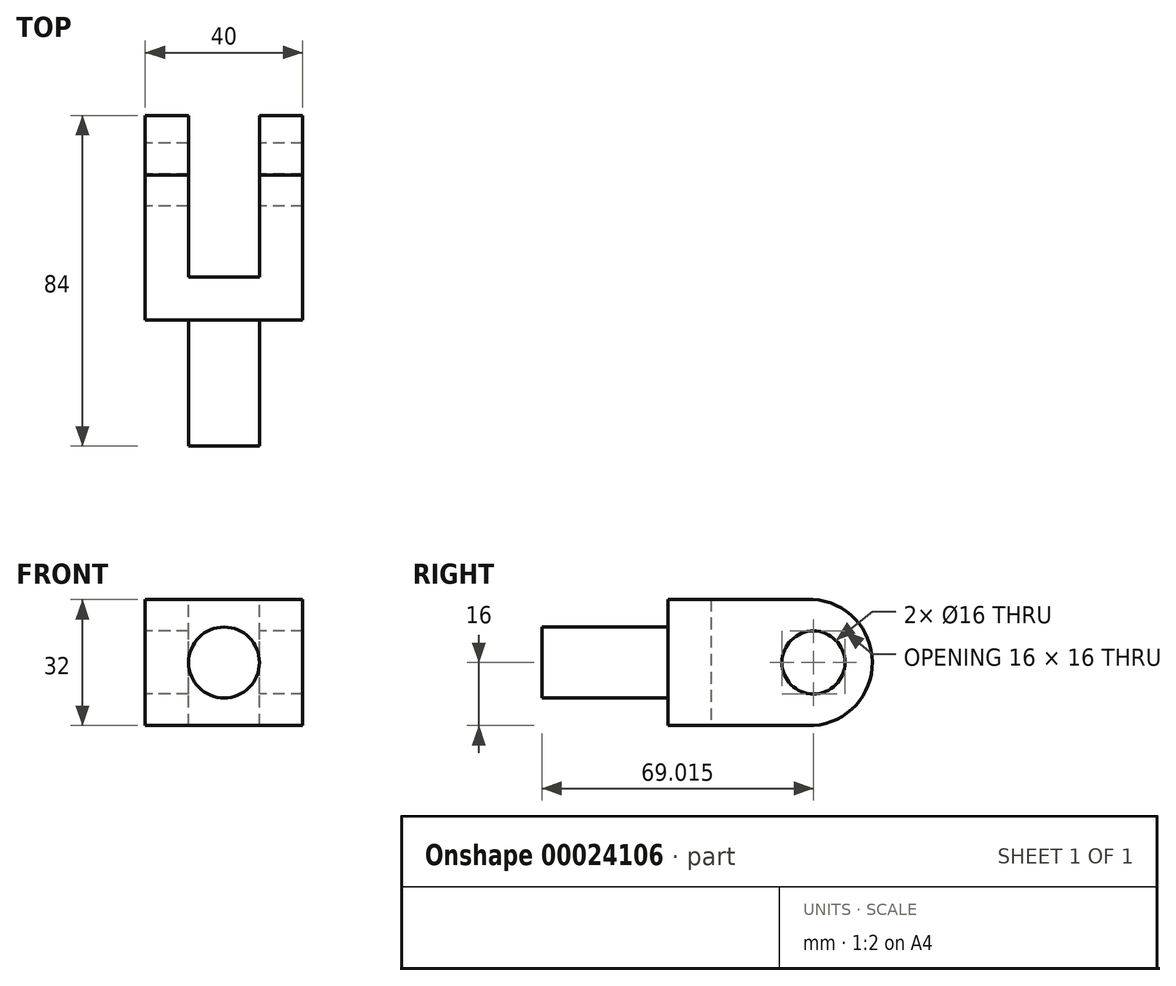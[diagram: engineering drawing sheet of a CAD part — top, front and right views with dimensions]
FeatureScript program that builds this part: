
annotation { "Feature Type Name" : "Feature", "Feature Type Description" : "" }
export const myFeature = defineFeature(function(context is Context, id is Id, definition is map)
    precondition{}
    {
        {
            var Q0;
            Q0=qCreatedBy(makeId("Top.planeOp"),FACE);
            var sketch = newSketch(context, id + "F0", { "sketchPlane" : qUnion([Q0])});
            skLineSegment(sketch, "E0", {"start": v(-30.3, 35) * mm, "end": v(-30.3, -17) * mm});
            skLineSegment(sketch, "E1", {"start": v(-30.3, -17) * mm, "end": v(9.7, -17) * mm});
            skLineSegment(sketch, "E2", {"start": v(9.7, -17) * mm, "end": v(9.7, 35) * mm});
            skLineSegment(sketch, "E3", {"start": v(-30.3, 35) * mm, "end": v(-19.3, 35) * mm});
            skLineSegment(sketch, "E4", {"start": v(9.7, 35) * mm, "end": v(-1.3, 35) * mm});
            skLineSegment(sketch, "E5", {"start": v(-19.3, 35) * mm, "end": v(-19.3, -6) * mm});
            skLineSegment(sketch, "E6", {"start": v(-1.3, 35) * mm, "end": v(-1.3, -6) * mm});
            skLineSegment(sketch, "E7", {"start": v(-19.3, -6) * mm, "end": v(-1.3, -6) * mm});
            skSolve(sketch);
        }
        {
            var Q0;
            Q0=qSketchRegion(id+"F0",true);
            extrude(context, id + "F1", {"entities" : qUnion([Q0]), "depth" : 32 * mm});
        }
        {
            var Q0;
            Q0=makeQuery(id+"F1.opExtrude","SWEPT_FACE",FACE,{"disambiguationData":[OSD([sQuery(id+"F0.wireOp",EDGE,"E0")])]});
            var sketch = newSketch(context, id + "F2", { "sketchPlane" : qUnion([Q0])});
            skCircle(sketch, "E8", {"center": v(-18.96, 16) * mm, "radius": 16.03 * mm});
            skPoint(sketch, "E8.first.point", {"position": v(-19.87, 32) * mm});
            skPoint(sketch, "E8.second.point", {"position": v(-35, 16) * mm});
            skPoint(sketch, "E8.third.point", {"position": v(-17.78, 0) * mm});
            skSolve(sketch);
        }
        {
            var Q0;
            {var subQ0=sQuery(id+"F0.wireOp",EDGE,"E0");var subQ1=makeQuery(id+"F1.opExtrude","CAP_EDGE",EDGE,{"disambiguationData":[OSD([subQ0])],"isStart":false});var subQ2=sQuery(id+"F2.wireOp",EDGE,"E8");var subQ3=makeQuery(id+"F2.imprint","INTERSECT",VERTEX,{"disambiguationData":[OD(0.0)],"derivedFrom":[subQ1,subQ2]});Q0=makeQuery(id+"F2.imprint","IMPRINT",FACE,{"disambiguationData":[TD([[makeQuery(id+"F2.imprint","IMPRINT",EDGE,{"disambiguationData":[TD([[subQ3,-1.0]])],"derivedFrom":subQ2}),-1.0]])]});}
            var Q1;
            {var subQ0=sQuery(id+"F0.wireOp",EDGE,"E0");var subQ1=makeQuery(id+"F1.opExtrude","CAP_EDGE",EDGE,{"disambiguationData":[OSD([subQ0])],"isStart":true});var subQ2=sQuery(id+"F2.wireOp",EDGE,"E8");var subQ3=makeQuery(id+"F2.imprint","INTERSECT",VERTEX,{"disambiguationData":[OD(0.0)],"derivedFrom":[subQ1,subQ2]});Q1=makeQuery(id+"F2.imprint","IMPRINT",FACE,{"disambiguationData":[TD([[makeQuery(id+"F2.imprint","IMPRINT",EDGE,{"disambiguationData":[TD([[subQ3,1.0]])],"derivedFrom":subQ2}),-1.0]])]});}
            extrude(context, id + "F3", {"entities" : qUnion([Q0, Q1]), "operationType" : NewBodyOperationType.REMOVE, "endBound" : BoundingType.THROUGH_ALL, "oppositeDirection" : true, "depth" : 25 * mm});
        }
        {
            var Q0;
            Q0=makeQuery(id+"F1.opExtrude","SWEPT_FACE",FACE,{"disambiguationData":[OSD([sQuery(id+"F0.wireOp",EDGE,"E0")])]});
            var sketch = newSketch(context, id + "F4", { "sketchPlane" : qUnion([Q0])});
            skCircle(sketch, "E9", {"center": v(-20, 16) * mm, "radius": 8 * mm});
            skSolve(sketch);
        }
        {
            var Q0;
            Q0=makeQuery(id+"F4.imprint","IMPRINT",FACE,{"disambiguationData":[TD([[makeQuery(id+"F4.imprint","IMPRINT",EDGE,{"derivedFrom":sQuery(id+"F4.wireOp",EDGE,"E9")}),1.0]])]});
            extrude(context, id + "F5", {"entities" : qUnion([Q0]), "operationType" : NewBodyOperationType.REMOVE, "endBound" : BoundingType.THROUGH_ALL, "oppositeDirection" : true, "depth" : 25 * mm});
        }
        {
            var Q0;
            Q0=makeQuery(id+"F1.opExtrude","SWEPT_FACE",FACE,{"disambiguationData":[OSD([sQuery(id+"F0.wireOp",EDGE,"E1")])]});
            var sketch = newSketch(context, id + "F6", { "sketchPlane" : qUnion([Q0])});
            skLineSegment(sketch, "E10", {"start": v(-10.3, 32) * mm, "end": v(-10.3, 0) * mm, "construction": true});
            skLineSegment(sketch, "E11", {"start": v(-10.3, 0) * mm, "end": v(-30.3, 16) * mm, "construction": true});
            skLineSegment(sketch, "E12", {"start": v(-30.3, 16) * mm, "end": v(9.7, 16) * mm, "construction": true});
            skLineSegment(sketch, "E13", {"start": v(9.7, 16) * mm, "end": v(-10.3, 0) * mm, "construction": true});
            skLineSegment(sketch, "E14", {"start": v(-10.3, 32) * mm, "end": v(-30.3, 16) * mm, "construction": true});
            skLineSegment(sketch, "E15", {"start": v(-10.3, 32) * mm, "end": v(9.7, 16) * mm, "construction": true});
            skCircle(sketch, "E16", {"center": v(-10.3, 16) * mm, "radius": 9 * mm});
            skSolve(sketch);
        }
        {
            var Q0;
            Q0=makeQuery(id+"F6.imprint","IMPRINT",FACE,{"disambiguationData":[TD([[makeQuery(id+"F6.imprint","IMPRINT",EDGE,{"derivedFrom":sQuery(id+"F6.wireOp",EDGE,"E16")}),1.0]])]});
            extrude(context, id + "F7", {"entities" : qUnion([Q0]), "operationType" : NewBodyOperationType.ADD, "depth" : 32 * mm});
        }
    });
